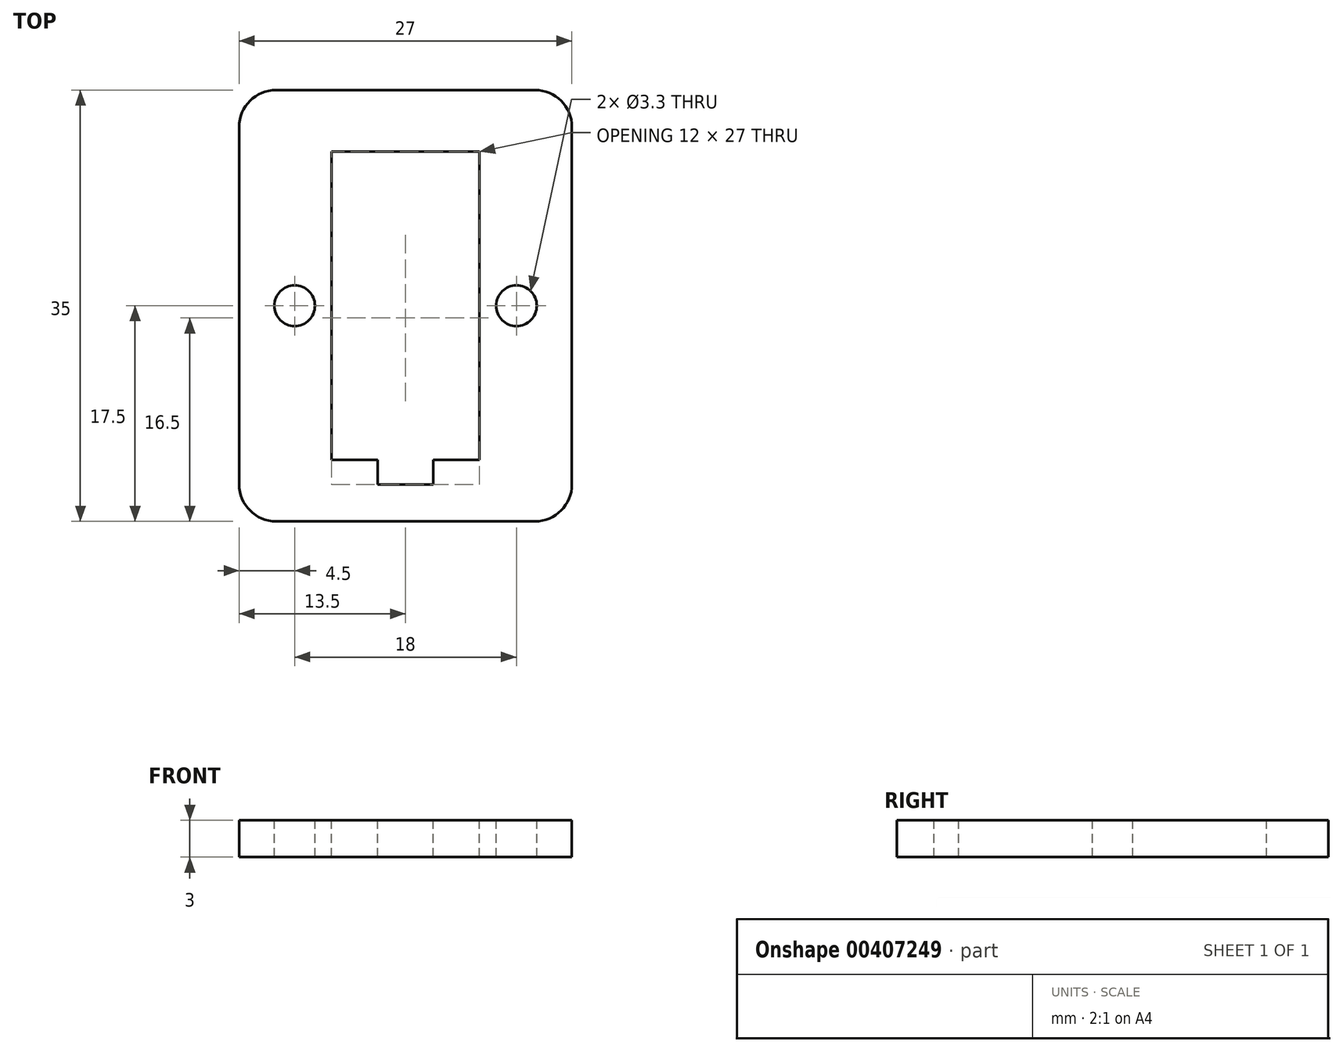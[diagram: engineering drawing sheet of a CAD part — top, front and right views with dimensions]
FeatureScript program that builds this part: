
annotation { "Feature Type Name" : "Feature", "Feature Type Description" : "" }
export const myFeature = defineFeature(function(context is Context, id is Id, definition is map)
    precondition{}
    {
        {
            var Q0;
            Q0=qCreatedBy(makeId("Top.planeOp"),FACE);
            var sketch = newSketch(context, id + "F0", { "sketchPlane" : qUnion([Q0])});
            skLineSegment(sketch, "E0.bottom", {"start": v(-10.5, 17.5) * mm, "end": v(10.5, 17.5) * mm});
            skLineSegment(sketch, "E0.top", {"start": v(-10.5, -17.5) * mm, "end": v(10.5, -17.5) * mm});
            skLineSegment(sketch, "E0.left", {"start": v(-13.5, 14.5) * mm, "end": v(-13.5, -14.5) * mm});
            skLineSegment(sketch, "E0.right", {"start": v(13.5, 14.5) * mm, "end": v(13.5, -14.5) * mm});
            skPoint(sketch, "E0.middle", {"position": v(0, 0) * mm});
            skPoint(sketch, "E1.visualSharp", {"position": v(-13.5, 17.5) * mm});
            skArc(sketch, "E1.filletArc", {"start": v(-10.5, 17.5) * mm, "mid": v(-12.62, 16.62) * mm, "end": v(-13.5, 14.5) * mm});
            skPoint(sketch, "E2.visualSharp", {"position": v(13.5, 17.5) * mm});
            skArc(sketch, "E2.filletArc", {"start": v(13.5, 14.5) * mm, "mid": v(12.62, 16.62) * mm, "end": v(10.5, 17.5) * mm});
            skPoint(sketch, "E3.visualSharp", {"position": v(13.5, -17.5) * mm});
            skArc(sketch, "E3.filletArc", {"start": v(10.5, -17.5) * mm, "mid": v(12.62, -16.62) * mm, "end": v(13.5, -14.5) * mm});
            skPoint(sketch, "E4.visualSharp", {"position": v(-13.5, -17.5) * mm});
            skArc(sketch, "E4.filletArc", {"start": v(-13.5, -14.5) * mm, "mid": v(-12.62, -16.62) * mm, "end": v(-10.5, -17.5) * mm});
            skSolve(sketch);
        }
        {
            var Q0;
            Q0=qSketchRegion(id+"F0",true);
            extrude(context, id + "F1", {"entities" : qUnion([Q0]), "depth" : 3 * mm});
        }
        {
            var Q0;
            Q0=makeQuery(id+"F1.opExtrude","CAP_FACE",FACE,{"disambiguationData":[OSD([sQuery(id+"F0.wireOp",EDGE,"E0.bottom"),sQuery(id+"F0.wireOp",EDGE,"E0.top"),sQuery(id+"F0.wireOp",EDGE,"E0.left"),sQuery(id+"F0.wireOp",EDGE,"E0.right"),sQuery(id+"F0.wireOp",EDGE,"E1.filletArc"),sQuery(id+"F0.wireOp",EDGE,"E2.filletArc"),sQuery(id+"F0.wireOp",EDGE,"E3.filletArc"),sQuery(id+"F0.wireOp",EDGE,"E4.filletArc")])],"isStart":false});
            var sketch = newSketch(context, id + "F2", { "sketchPlane" : qUnion([Q0])});
            skCircle(sketch, "E5", {"center": v(-9, 0) * mm, "radius": 1.65 * mm});
            skCircle(sketch, "E6", {"center": v(9, 0) * mm, "radius": 1.65 * mm});
            skSolve(sketch);
        }
        {
            var Q0;
            Q0=sQuery(id+"F2.wireOp",VERTEX,"E5.center");
            var Q1;
            Q1=sQuery(id+"F2.wireOp",VERTEX,"E6.center");
            var Q2;
            Q2=makeQuery(id+"F1.opExtrude","SWEPT_BODY",BODY,{"disambiguationData":[OSD([sQuery(id+"F0.wireOp",EDGE,"E0.bottom"),sQuery(id+"F0.wireOp",EDGE,"E0.top"),sQuery(id+"F0.wireOp",EDGE,"E0.left"),sQuery(id+"F0.wireOp",EDGE,"E0.right"),sQuery(id+"F0.wireOp",EDGE,"E1.filletArc"),sQuery(id+"F0.wireOp",EDGE,"E2.filletArc"),sQuery(id+"F0.wireOp",EDGE,"E3.filletArc"),sQuery(id+"F0.wireOp",EDGE,"E4.filletArc")])]});
            hole(context, id + "F3", {"style" : HoleStyle.SIMPLE, "endStyle" : HoleEndStyle.THROUGH, "holeDiameter" : 3.3 * mm, "locations" : qUnion([Q0, Q1]), "scope" : qUnion([Q2]), "isTappedThrough" : true});
        }
        {
            var Q0;
            Q0=makeQuery(id+"F1.opExtrude","CAP_FACE",FACE,{"disambiguationData":[OSD([sQuery(id+"F0.wireOp",EDGE,"E0.bottom"),sQuery(id+"F0.wireOp",EDGE,"E0.top"),sQuery(id+"F0.wireOp",EDGE,"E0.left"),sQuery(id+"F0.wireOp",EDGE,"E0.right"),sQuery(id+"F0.wireOp",EDGE,"E1.filletArc"),sQuery(id+"F0.wireOp",EDGE,"E2.filletArc"),sQuery(id+"F0.wireOp",EDGE,"E3.filletArc"),sQuery(id+"F0.wireOp",EDGE,"E4.filletArc")])],"isStart":false});
            var sketch = newSketch(context, id + "F4", { "sketchPlane" : qUnion([Q0])});
            skLineSegment(sketch, "E7.bottom", {"start": v(-6, 12.5) * mm, "end": v(6, 12.5) * mm});
            skLineSegment(sketch, "E7.top", {"start": v(-6, -12.5) * mm, "end": v(-2.25, -12.5) * mm});
            skLineSegment(sketch, "E7.left", {"start": v(-6, 12.5) * mm, "end": v(-6, -12.5) * mm});
            skLineSegment(sketch, "E7.right", {"start": v(6, 12.5) * mm, "end": v(6, -12.5) * mm});
            skPoint(sketch, "E7.middle", {"position": v(0, 0) * mm});
            skLineSegment(sketch, "E8.bottom", {"start": v(-2.25, -14.5) * mm, "end": v(2.25, -14.5) * mm});
            skLineSegment(sketch, "E8.left", {"start": v(-2.25, -14.5) * mm, "end": v(-2.25, -12.5) * mm});
            skLineSegment(sketch, "E8.right", {"start": v(2.25, -14.5) * mm, "end": v(2.25, -12.5) * mm});
            skLineSegment(sketch, "E9.trimOffspring", {"start": v(2.25, -12.5) * mm, "end": v(6, -12.5) * mm});
            skSolve(sketch);
        }
        {
            var Q0;
            Q0 = qSketchRegion(id + "F4", true);
            extrude(context, id + "F5", {"entities" : qUnion([Q0]), "operationType" : NewBodyOperationType.REMOVE, "oppositeDirection" : true, "depth" : 25 * mm});
        }
    });
